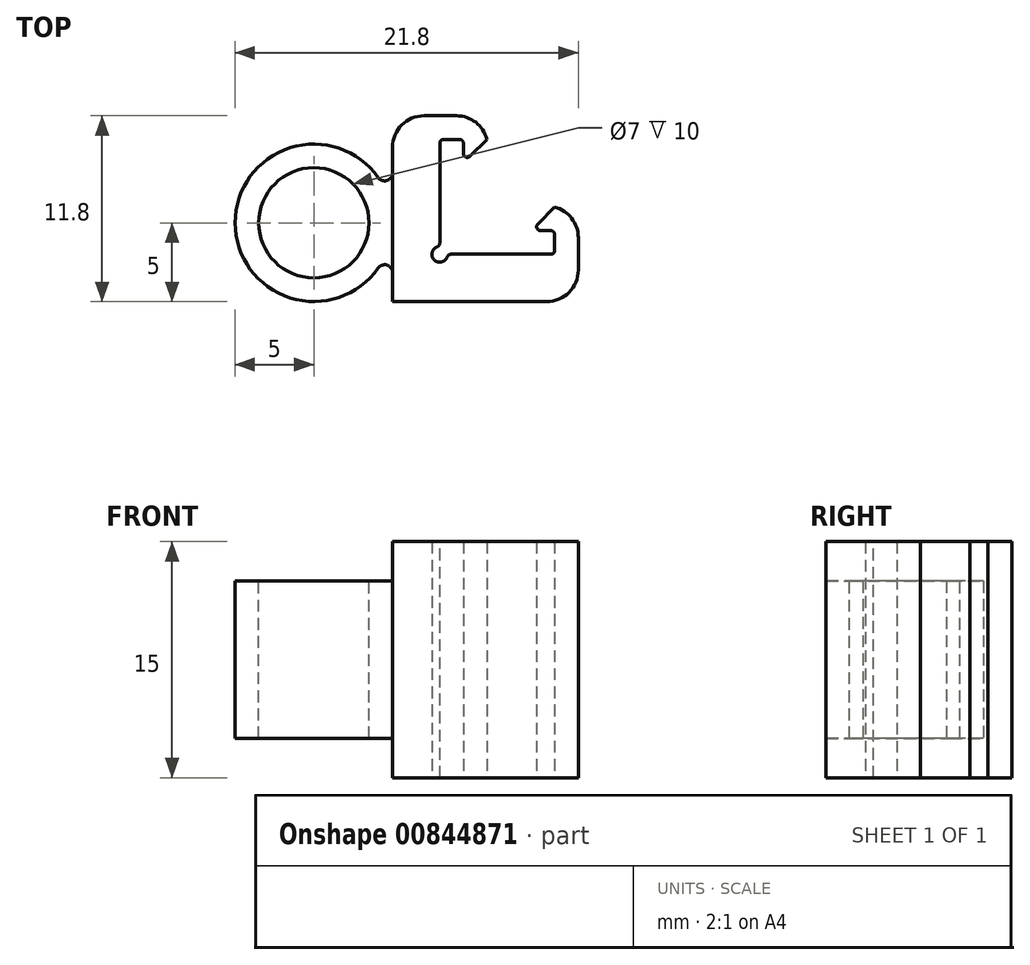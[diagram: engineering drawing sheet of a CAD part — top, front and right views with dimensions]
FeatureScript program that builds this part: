
annotation { "Feature Type Name" : "Feature", "Feature Type Description" : "" }
export const myFeature = defineFeature(function(context is Context, id is Id, definition is map)
    precondition{}
    {
        {
            var Q0;
            Q0=qCreatedBy(makeId("Top.planeOp"),FACE);
            var sketch = newSketch(context, id + "F0", { "sketchPlane" : qUnion([Q0])});
            skLineSegment(sketch, "E0", {"start": v(0, 11.8) * mm, "end": v(0, 0) * mm});
            skLineSegment(sketch, "E1", {"start": v(0, 0) * mm, "end": v(11.8, 0) * mm});
            skLineSegment(sketch, "E2", {"start": v(11.8, 0) * mm, "end": v(11.8, 3) * mm});
            skLineSegment(sketch, "E3", {"start": v(10.3, 3) * mm, "end": v(3, 3) * mm});
            skLineSegment(sketch, "E4", {"start": v(3, 3) * mm, "end": v(3, 10.3) * mm});
            skLineSegment(sketch, "E5", {"start": v(3, 11.8) * mm, "end": v(0, 11.8) * mm});
            skLineSegment(sketch, "E6", {"start": v(3, 11.8) * mm, "end": v(6, 11.8) * mm});
            skLineSegment(sketch, "E7", {"start": v(6, 11.8) * mm, "end": v(6, 10.3) * mm});
            skLineSegment(sketch, "E8", {"start": v(6, 10.3) * mm, "end": v(4.5, 8.8) * mm});
            skLineSegment(sketch, "E9", {"start": v(4.5, 8.8) * mm, "end": v(4.5, 10.3) * mm});
            skLineSegment(sketch, "E10", {"start": v(4.5, 10.3) * mm, "end": v(3, 10.3) * mm});
            skArc(sketch, "E11", {"start": v(3, 3.5) * mm, "mid": v(2.65, 2.65) * mm, "end": v(3.5, 3) * mm});
            skLineSegment(sketch, "E12", {"start": v(10.3, 3) * mm, "end": v(10.3, 4.5) * mm});
            skLineSegment(sketch, "E13", {"start": v(10.3, 6) * mm, "end": v(11.8, 6) * mm});
            skLineSegment(sketch, "E14", {"start": v(11.8, 6) * mm, "end": v(11.8, 3) * mm});
            skLineSegment(sketch, "E15", {"start": v(10.3, 6) * mm, "end": v(8.8, 4.5) * mm});
            skLineSegment(sketch, "E16", {"start": v(8.8, 4.5) * mm, "end": v(10.3, 4.5) * mm});
            skSolve(sketch);
        }
        {
            var Q0;
            Q0=makeQuery(id+"F0.imprint","IMPRINT",FACE,{"disambiguationData":[TD([[makeQuery(id+"F0.imprint","IMPRINT",EDGE,{"derivedFrom":sQuery(id+"F0.wireOp",EDGE,"E0")}),1.0]])]});
            extrude(context, id + "F1", {"entities" : qUnion([Q0]), "depth" : 15 * mm, "offsetDistance" : 25.4 * mm});
        }
        {
            var Q0;
            Q0=makeQuery(id+"F1.opExtrude","SWEPT_EDGE",EDGE,{"disambiguationData":[OSD([sQuery(id+"F0.wireOp",EDGE,"E0"),sQuery(id+"F0.wireOp",EDGE,"E5")])]});
            var Q1;
            Q1=makeQuery(id+"F1.opExtrude","SWEPT_EDGE",EDGE,{"disambiguationData":[OSD([sQuery(id+"F0.wireOp",EDGE,"E6"),sQuery(id+"F0.wireOp",EDGE,"E7")])]});
            var Q2;
            Q2=makeQuery(id+"F1.opExtrude","SWEPT_EDGE",EDGE,{"disambiguationData":[OSD([sQuery(id+"F0.wireOp",EDGE,"E1"),sQuery(id+"F0.wireOp",EDGE,"E2")])]});
            var Q3;
            Q3=makeQuery(id+"F1.opExtrude","SWEPT_EDGE",EDGE,{"disambiguationData":[OSD([sQuery(id+"F0.wireOp",EDGE,"E13"),sQuery(id+"F0.wireOp",EDGE,"E14")])]});
            fillet(context, id + "F2", {"entities" : qUnion([Q0, Q1, Q2, Q3]), "radius" : 2 * mm, "tangentPropagation" : true, "allowEdgeOverflow" : false});
        }
        {
            var Q0;
            Q0=makeQuery(id+"F1.opExtrude","SWEPT_EDGE",EDGE,{"disambiguationData":[OSD([sQuery(id+"F0.wireOp",EDGE,"E3"),sQuery(id+"F0.wireOp",EDGE,"795089ed-91bf-4bf5-bc84-0bb3afbf4238.0")])]});
            var Q1;
            Q1=makeQuery(id+"F1.opExtrude","SWEPT_EDGE",EDGE,{"disambiguationData":[OSD([sQuery(id+"F0.wireOp",EDGE,"E4"),sQuery(id+"F0.wireOp",EDGE,"E10")])]});
            var Q2;
            Q2=makeQuery(id+"F1.opExtrude","SWEPT_EDGE",EDGE,{"disambiguationData":[OSD([sQuery(id+"F0.wireOp",EDGE,"E9"),sQuery(id+"F0.wireOp",EDGE,"E10")])]});
            var Q3;
            Q3=makeQuery(id+"F1.opExtrude","SWEPT_EDGE",EDGE,{"disambiguationData":[OSD([sQuery(id+"F0.wireOp",EDGE,"795089ed-91bf-4bf5-bc84-0bb3afbf4238.0"),sQuery(id+"F0.wireOp",EDGE,"O1gMg828-a2S5-aLbF-4dkx-ozUuB1Kks5ro")])]});
            var Q4;
            Q4=makeQuery(id+"F1.opExtrude","SWEPT_EDGE",EDGE,{"disambiguationData":[OSD([sQuery(id+"F0.wireOp",EDGE,"6d239e18-aa0d-44d8-89d8-2559cdf57522"),sQuery(id+"F0.wireOp",EDGE,"O1gMg828-a2S5-aLbF-4dkx-ozUuB1Kks5ro")])]});
            var Q5;
            Q5=makeQuery(id+"F1.opExtrude","SWEPT_EDGE",EDGE,{"disambiguationData":[OSD([sQuery(id+"F0.wireOp",EDGE,"E8"),sQuery(id+"F0.wireOp",EDGE,"E9")])]});
            var Q6;
            Q6=makeQuery(id+"F1.opExtrude","SWEPT_EDGE",EDGE,{"disambiguationData":[OSD([sQuery(id+"F0.wireOp",EDGE,"E4"),sQuery(id+"F0.wireOp",EDGE,"E11")])]});
            var Q7;
            Q7=makeQuery(id+"F1.opExtrude","SWEPT_EDGE",EDGE,{"disambiguationData":[OSD([sQuery(id+"F0.wireOp",EDGE,"E3"),sQuery(id+"F0.wireOp",EDGE,"E11")])]});
            var Q8;
            Q8=makeQuery(id+"F1.opExtrude","SWEPT_EDGE",EDGE,{"disambiguationData":[OSD([sQuery(id+"F0.wireOp",EDGE,"E12"),sQuery(id+"F0.wireOp",EDGE,"E16")])]});
            var Q9;
            Q9=makeQuery(id+"F1.opExtrude","SWEPT_EDGE",EDGE,{"disambiguationData":[OSD([sQuery(id+"F0.wireOp",EDGE,"E15"),sQuery(id+"F0.wireOp",EDGE,"E16")])]});
            fillet(context, id + "F3", {"entities" : qUnion([Q0, Q1, Q2, Q3, Q4, Q5, Q6, Q7, Q8, Q9]), "radius" : 0.25 * mm, "tangentPropagation" : true, "allowEdgeOverflow" : false});
        }
        {
            var Q0;
            Q0=qCreatedBy(makeId("Top.planeOp"),FACE);
            var Q1;
            Q1=makeQuery(id+"F1.opExtrude","CAP_FACE",FACE,{"disambiguationData":[OSD([sQuery(id+"F0.wireOp",EDGE,"E0"),sQuery(id+"F0.wireOp",EDGE,"E1"),sQuery(id+"F0.wireOp",EDGE,"E2"),sQuery(id+"F0.wireOp",EDGE,"E3"),sQuery(id+"F0.wireOp",EDGE,"E4"),sQuery(id+"F0.wireOp",EDGE,"E5"),sQuery(id+"F0.wireOp",EDGE,"6d239e18-aa0d-44d8-89d8-2559cdf57522"),sQuery(id+"F0.wireOp",EDGE,"795089ed-91bf-4bf5-bc84-0bb3afbf4238.0"),sQuery(id+"F0.wireOp",EDGE,"O1gMg828-a2S5-aLbF-4dkx-ozUuB1Kks5ro"),sQuery(id+"F0.wireOp",EDGE,"E6"),sQuery(id+"F0.wireOp",EDGE,"E7"),sQuery(id+"F0.wireOp",EDGE,"E8"),sQuery(id+"F0.wireOp",EDGE,"E9"),sQuery(id+"F0.wireOp",EDGE,"E10"),sQuery(id+"F0.wireOp",EDGE,"E11")])],"isStart":false});
            cPlane(context, id + "F4", {"entities" : qUnion([Q0, Q1]), "cplaneType" : CPlaneType.MID_PLANE, "offset" : 25.4 * mm, "width" : 152.4 * mm, "height" : 152.4 * mm});
        }
        {
            var Q0;
            Q0=qCreatedBy(id+"F4.planeOp",FACE);
            var sketch = newSketch(context, id + "F5", { "sketchPlane" : qUnion([Q0])});
            skCircle(sketch, "E17", {"center": v(-5, 5) * mm, "radius": 5 * mm});
            skLineSegment(sketch, "E18.0", {"start": v(0, 9.8) * mm, "end": v(0, 0) * mm});
            skLineSegment(sketch, "E19.0", {"start": v(0, 0) * mm, "end": v(9.8, 0) * mm});
            skCircle(sketch, "E20", {"center": v(-0.5, 1.84) * mm, "radius": 0.5 * mm});
            skCircle(sketch, "E21", {"center": v(-0.5, 8.16) * mm, "radius": 0.5 * mm});
            skSolve(sketch);
        }
        {
            var Q0;
            {var subQ0=sQuery(id+"F5.wireOp",EDGE,"E17");var subQ1=makeQuery(id+"F5.imprint","INTERSECT",VERTEX,{"derivedFrom":[subQ0,sQuery(id+"F5.wireOp",EDGE,"E21")]});Q0=makeQuery(id+"F5.imprint","IMPRINT",FACE,{"disambiguationData":[TD([[makeQuery(id+"F5.imprint","IMPRINT",EDGE,{"disambiguationData":[TD([[subQ1,1.0]])],"derivedFrom":subQ0}),1.0]])]});}
            var Q1;
            {var subQ0=sQuery(id+"F5.wireOp",EDGE,"E18.0");var subQ1=sQuery(id+"F5.wireOp",EDGE,"E17");var subQ2=makeQuery(id+"F5.imprint","INTERSECT",VERTEX,{"derivedFrom":[subQ1,subQ0]});Q1=makeQuery(id+"F5.imprint","IMPRINT",FACE,{"disambiguationData":[TD([[makeQuery(id+"F5.imprint","IMPRINT",EDGE,{"disambiguationData":[TD([[subQ2,1.0]])],"derivedFrom":subQ1}),-1.0]])]});}
            var Q2;
            {var subQ0=sQuery(id+"F5.wireOp",EDGE,"E21");var subQ1=sQuery(id+"F5.wireOp",EDGE,"E17");var subQ2=makeQuery(id+"F5.imprint","INTERSECT",VERTEX,{"derivedFrom":[subQ1,subQ0]});Q2=makeQuery(id+"F5.imprint","IMPRINT",FACE,{"disambiguationData":[TD([[makeQuery(id+"F5.imprint","IMPRINT",EDGE,{"disambiguationData":[TD([[subQ2,1.0]])],"derivedFrom":subQ1}),-1.0]])]});}
            extrude(context, id + "F6", {"entities" : qUnion([Q0, Q1, Q2]), "operationType" : NewBodyOperationType.ADD, "endBound" : BoundingType.SYMMETRIC, "depth" : 10 * mm, "offsetDistance" : 25.4 * mm});
        }
        {
            var Q0;
            Q0=qCreatedBy(id+"F4.planeOp",FACE);
            var sketch = newSketch(context, id + "F7", { "sketchPlane" : qUnion([Q0])});
            skCircle(sketch, "E22", {"center": v(-5, 5) * mm, "radius": 3.5 * mm});
            skLineSegment(sketch, "E23.0", {"start": v(-0.9, 7.87) * mm, "end": v(-0.9, 7.87) * mm});
            skSolve(sketch);
        }
        {
            var Q0;
            Q0 = qSketchRegion(id + "F7", true);
            extrude(context, id + "F8", {"entities" : qUnion([Q0]), "operationType" : NewBodyOperationType.REMOVE, "endBound" : BoundingType.THROUGH_ALL, "oppositeDirection" : true, "depth" : 15 * mm, "offsetDistance" : 25.4 * mm, "hasSecondDirection" : true, "secondDirectionBound" : SecondDirectionBoundingType.THROUGH_ALL, "secondDirectionOppositeDirection" : false, "secondDirectionDepth" : 25.4 * mm});
        }
    });
